# Revit family: Hand-Shower-Set_Contemporary_Soiree_TS960H_TOTO
name_source: partatom
category: Plumbing Fixtures
revit_build: Autodesk Revit Architecture 2013 (Build: 20130531_2115(x64)
units: mm (PartAtom-declared; Revit-internal decimal feet)

## types (1)
- TS960H
    04 CSI = 22 41 39
    95 CSI = 15416
    Assembly Code = D2010710
    CAD Drawing URL = http://assets.totousa.com
    CW Connection = No
    CWFU = 0
    Color Availability = #CP Polished Chrome, #BN Brushed Nickel, #PN Polished Nickel
    Default Elevation = 48"
    Depth = 4 1/8"
    Description = Handshower Set (with Slide Bar)
    Finish = Metal - TOTO - Chrome - Polished
    Flow Rate = 2.50 GPM
    HW Connection = No
    HWFU = 0
    Height = 31"
    Manufacturer = TOTO USA, Inc.
    Manufacturer Fax = (770) 282-0002
    Model = TS960H
    Series = Soiree
    Shipping Weight = 7.00 lb
    Spec Sheet URL = http://assets.totousa.com
    Style = Contemporary
    Subcategory = Showers
    TW Connector = Yes
    Tempered Water Connection NPT = 1"
    Tempered Water Connector = Tempered Water Connection
    Toto BIM Number = BM-00058
    URL = http://www.totousa.com
    Vent Connection = No
    WFU = 0
    Warranty = Lifetime Limited Warranty (Residential Use); One Year Limited (Commercial Use)
    Warranty URL = http://www.totousa.com
    Waste Connection = No
    Width = 9 3/4"

## geometry (parser evidence)
native form markers: Blend x6, Sweep x11
no freeform markers — native parametric forms only
